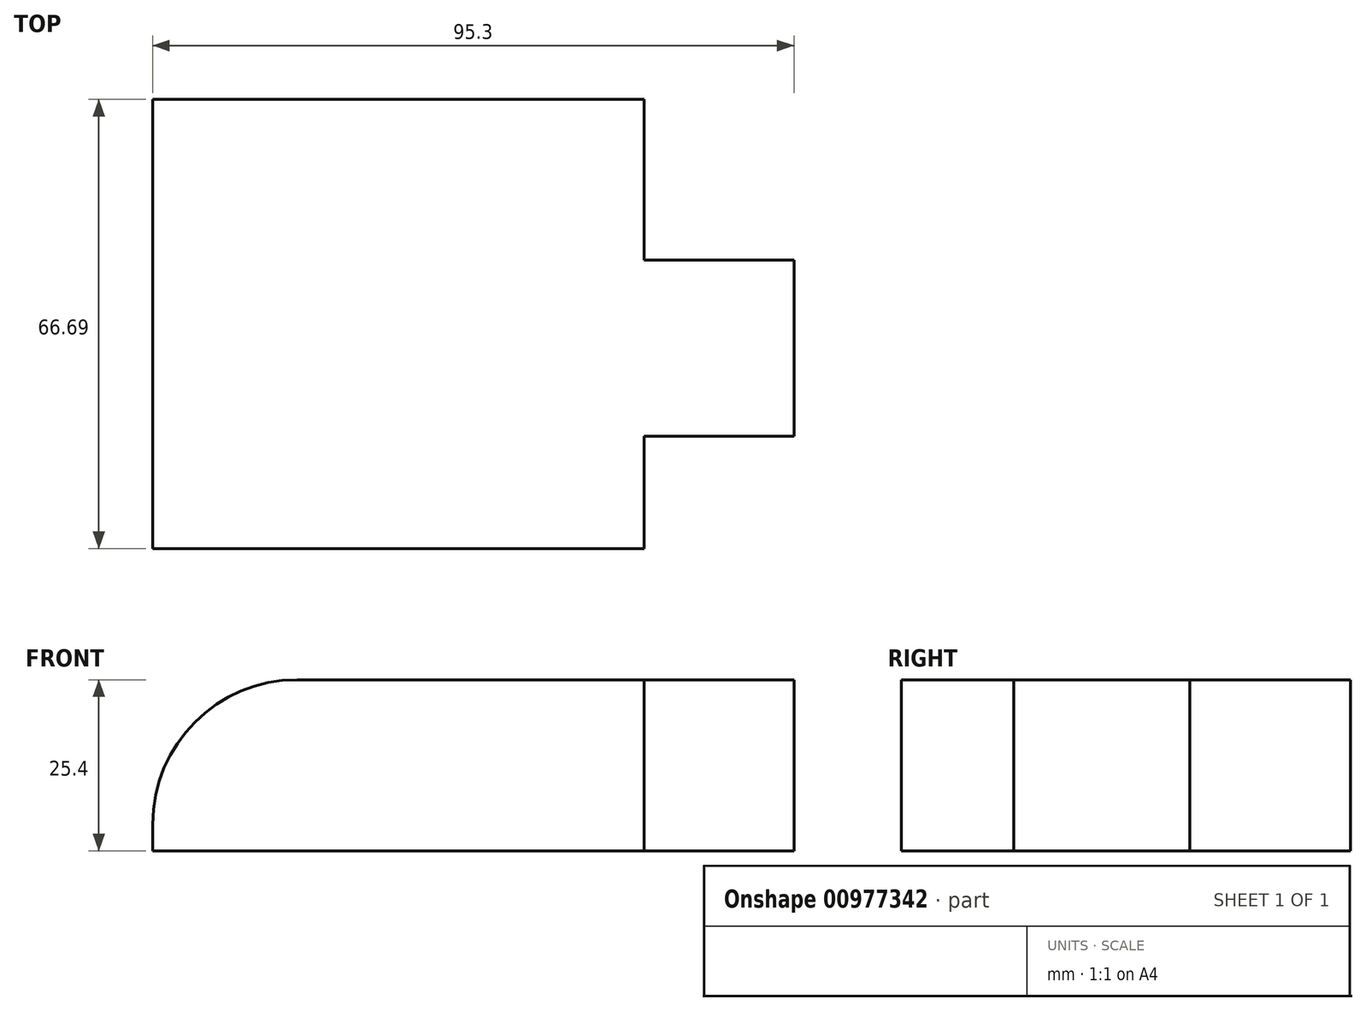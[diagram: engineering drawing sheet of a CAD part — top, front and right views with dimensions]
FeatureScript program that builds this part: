
annotation { "Feature Type Name" : "Feature", "Feature Type Description" : "" }
export const myFeature = defineFeature(function(context is Context, id is Id, definition is map)
    precondition{}
    {
        {
            var Q0;
            Q0=qCreatedBy(makeId("Top.planeOp"),FACE);
            var sketch = newSketch(context, id + "F0", { "sketchPlane" : qUnion([Q0])});
            skLineSegment(sketch, "E0.bottom", {"start": v(-64.5, -42.81) * mm, "end": v(8.52, -42.81) * mm});
            skLineSegment(sketch, "E0.top", {"start": v(-64.5, 23.88) * mm, "end": v(8.52, 23.88) * mm});
            skLineSegment(sketch, "E0.left", {"start": v(-64.5, -42.81) * mm, "end": v(-64.5, 23.88) * mm});
            skLineSegment(sketch, "E0.right", {"start": v(8.52, -42.81) * mm, "end": v(8.52, 23.88) * mm});
            skLineSegment(sketch, "E1.bottom", {"start": v(0, 0) * mm, "end": v(30.8, 0) * mm});
            skLineSegment(sketch, "E1.top", {"start": v(0, -26.15) * mm, "end": v(30.8, -26.15) * mm});
            skLineSegment(sketch, "E1.left", {"start": v(0, 0) * mm, "end": v(0, -26.15) * mm});
            skLineSegment(sketch, "E1.right", {"start": v(30.8, 0) * mm, "end": v(30.8, -26.15) * mm});
            skSolve(sketch);
        }
        {
            var Q0;
            Q0 = qSketchRegion(id + "F0", true);
            extrude(context, id + "F1", {"entities" : qUnion([Q0]), "depth" : 25.4 * mm, "offsetDistance" : 25.4 * mm});
        }
        {
            var Q0;
            Q0=makeQuery(id+"F1.opExtrude","CAP_EDGE",EDGE,{"disambiguationData":[OSD([sQuery(id+"F0.wireOp",EDGE,"E0.left")])],"isStart":false});
            fillet(context, id + "F2", {"entities" : qUnion([Q0]), "radius" : 21.46 * mm, "tangentPropagation" : true, "allowEdgeOverflow" : false});
        }
        {
            var Q0;
            Q0=makeQuery(id+"F1.opExtrude","CAP_FACE",FACE,{"disambiguationData":[OSD([sQuery(id+"F0.wireOp",EDGE,"E0.bottom"),sQuery(id+"F0.wireOp",EDGE,"E0.top"),sQuery(id+"F0.wireOp",EDGE,"E0.left"),sQuery(id+"F0.wireOp",EDGE,"E0.right"),sQuery(id+"F0.wireOp",EDGE,"E1.bottom"),sQuery(id+"F0.wireOp",EDGE,"E1.top"),sQuery(id+"F0.wireOp",EDGE,"E1.right")])],"isStart":false});
            var sketch = newSketch(context, id + "F3", { "sketchPlane" : qUnion([Q0])});
            skLineSegment(sketch, "E2.bottom", {"start": v(-32.58, -24.65) * mm, "end": v(-9.8, -24.65) * mm});
            skLineSegment(sketch, "E2.top", {"start": v(-32.58, 5.4) * mm, "end": v(-9.8, 5.4) * mm});
            skLineSegment(sketch, "E2.left", {"start": v(-32.58, -24.65) * mm, "end": v(-32.58, 5.4) * mm});
            skLineSegment(sketch, "E2.right", {"start": v(-9.8, -24.65) * mm, "end": v(-9.8, 5.4) * mm});
            skSolve(sketch);
        }
        {
            var Q0;
            Q0=makeQuery(id+"F3.imprint","IMPRINT",FACE,{"disambiguationData":[TD([[makeQuery(id+"F3.imprint","IMPRINT",EDGE,{"derivedFrom":sQuery(id+"F3.wireOp",EDGE,"E2.bottom")}),1.0]])]});
            extrude(context, id + "F4", {"entities" : qUnion([Q0]), "operationType" : NewBodyOperationType.ADD, "oppositeDirection" : true, "depth" : 3.8 * mm, "offsetDistance" : 25.4 * mm});
        }
    });
